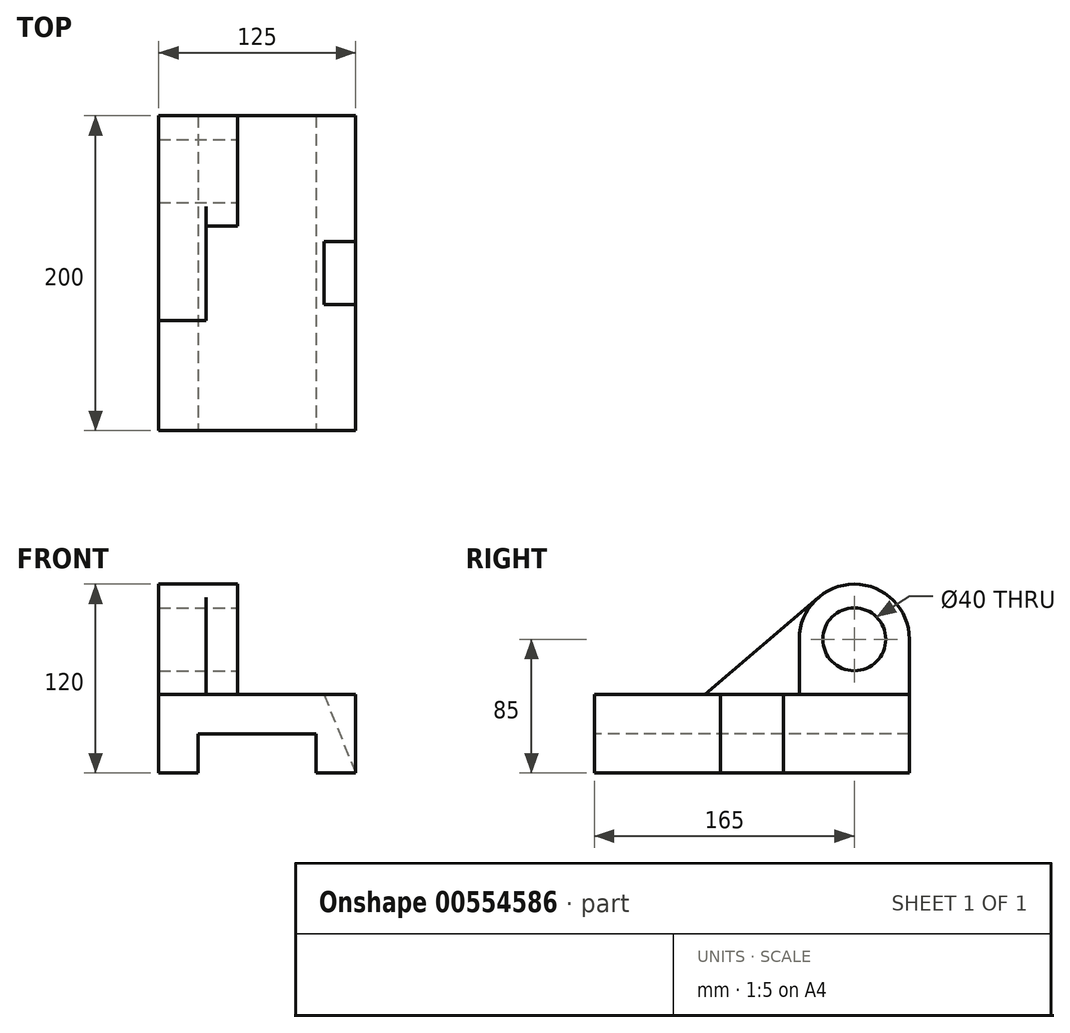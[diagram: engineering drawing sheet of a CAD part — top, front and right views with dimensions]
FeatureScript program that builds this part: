
annotation { "Feature Type Name" : "Feature", "Feature Type Description" : "" }
export const myFeature = defineFeature(function(context is Context, id is Id, definition is map)
    precondition{}
    {
        {
            var Q0;
            Q0=qCreatedBy(makeId("Top.planeOp"),FACE);
            var sketch = newSketch(context, id + "F0", { "sketchPlane" : qUnion([Q0])});
            skLineSegment(sketch, "E0.bottom", {"start": v(61.97, -78.78) * mm, "end": v(-63.03, -78.78) * mm});
            skLineSegment(sketch, "E0.top", {"start": v(61.97, 121.22) * mm, "end": v(-63.03, 121.22) * mm});
            skLineSegment(sketch, "E0.left", {"start": v(61.97, -78.78) * mm, "end": v(61.97, 121.22) * mm});
            skLineSegment(sketch, "E0.right", {"start": v(-63.03, -78.78) * mm, "end": v(-63.03, 121.22) * mm});
            skSolve(sketch);
        }
        {
            var Q0;
            Q0=makeQuery(id+"F0.imprint","IMPRINT",FACE,{"disambiguationData":[TD([[makeQuery(id+"F0.imprint","IMPRINT",EDGE,{"derivedFrom":sQuery(id+"F0.wireOp",EDGE,"E0.bottom")}),-1.0]])]});
            extrude(context, id + "F1", {"entities" : qUnion([Q0]), "depth" : 50 * mm, "offsetDistance" : 25 * mm});
        }
        {
            var Q0;
            Q0=makeQuery(id+"F1.opExtrude","CAP_FACE",FACE,{"disambiguationData":[OSD([sQuery(id+"F0.wireOp",EDGE,"E0.bottom"),sQuery(id+"F0.wireOp",EDGE,"E0.top"),sQuery(id+"F0.wireOp",EDGE,"E0.left"),sQuery(id+"F0.wireOp",EDGE,"E0.right")])],"isStart":false});
            var sketch = newSketch(context, id + "F2", { "sketchPlane" : qUnion([Q0])});
            skLineSegment(sketch, "E1.bottom", {"start": v(-63.03, 121.22) * mm, "end": v(-13.03, 121.22) * mm});
            skLineSegment(sketch, "E1.top", {"start": v(-63.03, 51.22) * mm, "end": v(-13.03, 51.22) * mm});
            skLineSegment(sketch, "E1.left", {"start": v(-63.03, 121.22) * mm, "end": v(-63.03, 51.22) * mm});
            skLineSegment(sketch, "E1.right", {"start": v(-13.03, 121.22) * mm, "end": v(-13.03, 51.22) * mm});
            skSolve(sketch);
        }
        {
            var Q0;
            Q0=makeQuery(id+"F2.imprint","IMPRINT",FACE,{"disambiguationData":[TD([[makeQuery(id+"F2.imprint","IMPRINT",EDGE,{"derivedFrom":sQuery(id+"F2.wireOp",EDGE,"E1.bottom")}),1.0]])]});
            extrude(context, id + "F3", {"entities" : qUnion([Q0]), "operationType" : NewBodyOperationType.ADD, "depth" : 35 * mm, "offsetDistance" : 25 * mm});
        }
        {
            var Q0;
            Q0=makeQuery(id+"F3.opExtrude","SWEPT_FACE",FACE,{"disambiguationData":[OSD([sQuery(id+"F2.wireOp",EDGE,"E1.right")])]});
            var sketch = newSketch(context, id + "F4", { "sketchPlane" : qUnion([Q0])});
            skCircle(sketch, "E2", {"center": v(86.22, 85) * mm, "radius": 35 * mm});
            skSolve(sketch);
        }
        {
            var Q0;
            {var subQ1=sQuery(id+"F2.wireOp",EDGE,"E1.right");var subQ2=makeQuery(id+"F3.opExtrude","CAP_EDGE",EDGE,{"disambiguationData":[OSD([subQ1])],"isStart":false});Q0=makeQuery(id+"F4.imprint","IMPRINT",FACE,{"disambiguationData":[TD([[makeQuery(id+"F4.imprint","IMPRINT",EDGE,{"derivedFrom":subQ2}),-1.0]])]});}
            extrude(context, id + "F5", {"entities" : qUnion([Q0]), "operationType" : NewBodyOperationType.ADD, "oppositeDirection" : true, "depth" : 50 * mm, "offsetDistance" : 25 * mm});
        }
        {
            var Q0;
            {var subQ0=sQuery(id+"F2.wireOp",EDGE,"E1.right");Q0=makeQuery(id+"F5.boolean.opBoolean","MERGE",FACE,{"derivedFrom":[makeQuery(id+"F3.opExtrude","SWEPT_FACE",FACE,{"disambiguationData":[OSD([subQ0])]}),makeQuery(id+"F5.opExtrude","CAP_FACE",FACE,{"disambiguationData":[OSD([subQ0,sQuery(id+"F4.wireOp",EDGE,"E2")])],"isStart":true})]});}
            var sketch = newSketch(context, id + "F6", { "sketchPlane" : qUnion([Q0])});
            skCircle(sketch, "E3", {"center": v(86.22, 85) * mm, "radius": 20 * mm});
            skSolve(sketch);
        }
        {
            var Q0;
            Q0=makeQuery(id+"F6.imprint","IMPRINT",FACE,{"disambiguationData":[TD([[makeQuery(id+"F6.imprint","IMPRINT",EDGE,{"derivedFrom":sQuery(id+"F6.wireOp",EDGE,"E3")}),1.0]])]});
            extrude(context, id + "F7", {"entities" : qUnion([Q0]), "operationType" : NewBodyOperationType.REMOVE, "endBound" : BoundingType.THROUGH_ALL, "oppositeDirection" : true, "depth" : 25 * mm, "offsetDistance" : 25 * mm});
        }
        {
            var Q0;
            Q0=makeQuery(id+"F5.boolean.opBoolean","MERGE",FACE,{"derivedFrom":[makeQuery(id+"F3.boolean.opBoolean","MERGE",FACE,{"derivedFrom":[makeQuery(id+"F1.opExtrude","SWEPT_FACE",FACE,{"disambiguationData":[OSD([sQuery(id+"F0.wireOp",EDGE,"E0.right")])]}),makeQuery(id+"F3.opExtrude","SWEPT_FACE",FACE,{"disambiguationData":[OSD([sQuery(id+"F2.wireOp",EDGE,"E1.left")])]})]}),makeQuery(id+"F5.opExtrude","CAP_FACE",FACE,{"disambiguationData":[OSD([sQuery(id+"F2.wireOp",EDGE,"E1.right"),sQuery(id+"F4.wireOp",EDGE,"E2")])],"isStart":false})]});
            var sketch = newSketch(context, id + "F8", { "sketchPlane" : qUnion([Q0])});
            skLineSegment(sketch, "E4", {"start": v(8.78, 50) * mm, "end": v(-63.51, 111.63) * mm});
            skSolve(sketch);
        }
        {
            var Q0;
            {var subQ0=sQuery(id+"F8.wireOp",EDGE,"E4");Q0=makeQuery(id+"F8.imprint","IMPRINT",FACE,{"disambiguationData":[TD([[makeQuery(id+"F8.imprint","IMPRINT",EDGE,{"derivedFrom":subQ0}),1.0]])]});}
            extrude(context, id + "F9", {"entities" : qUnion([Q0]), "operationType" : NewBodyOperationType.ADD, "oppositeDirection" : true, "depth" : 30 * mm, "offsetDistance" : 25 * mm});
        }
        {
            var Q0;
            Q0=makeQuery(id+"F1.opExtrude","SWEPT_FACE",FACE,{"disambiguationData":[OSD([sQuery(id+"F0.wireOp",EDGE,"E0.bottom")])]});
            var sketch = newSketch(context, id + "F10", { "sketchPlane" : qUnion([Q0])});
            skLineSegment(sketch, "E5.bottom", {"start": v(-38.03, 0) * mm, "end": v(36.97, 0) * mm});
            skLineSegment(sketch, "E5.top", {"start": v(-38.03, 25) * mm, "end": v(36.97, 25) * mm});
            skLineSegment(sketch, "E5.left", {"start": v(-38.03, 0) * mm, "end": v(-38.03, 25) * mm});
            skLineSegment(sketch, "E5.right", {"start": v(36.97, 0) * mm, "end": v(36.97, 25) * mm});
            skSolve(sketch);
        }
        {
            var Q0;
            Q0=makeQuery(id+"F10.imprint","IMPRINT",FACE,{"disambiguationData":[TD([[makeQuery(id+"F10.imprint","IMPRINT",EDGE,{"derivedFrom":sQuery(id+"F10.wireOp",EDGE,"E5.bottom")}),-1.0]])]});
            extrude(context, id + "F11", {"entities" : qUnion([Q0]), "operationType" : NewBodyOperationType.REMOVE, "endBound" : BoundingType.THROUGH_ALL, "oppositeDirection" : true, "depth" : 25 * mm, "offsetDistance" : 25 * mm});
        }
        {
            var Q0;
            Q0=makeQuery(id+"F1.opExtrude","SWEPT_FACE",FACE,{"disambiguationData":[OSD([sQuery(id+"F0.wireOp",EDGE,"E0.left")])]});
            var sketch = newSketch(context, id + "F12", { "sketchPlane" : qUnion([Q0])});
            skLineSegment(sketch, "E6.bottom", {"start": v(1.22, 0) * mm, "end": v(41.22, 0) * mm});
            skLineSegment(sketch, "E6.top", {"start": v(1.22, 50) * mm, "end": v(41.22, 50) * mm});
            skLineSegment(sketch, "E6.left", {"start": v(1.22, 0) * mm, "end": v(1.22, 50) * mm});
            skLineSegment(sketch, "E6.right", {"start": v(41.22, 0) * mm, "end": v(41.22, 50) * mm});
            skSolve(sketch);
        }
        {
            var Q0;
            Q0=makeQuery(id+"F12.imprint","IMPRINT",FACE,{"disambiguationData":[TD([[makeQuery(id+"F12.imprint","IMPRINT",EDGE,{"derivedFrom":sQuery(id+"F12.wireOp",EDGE,"E6.bottom")}),1.0]])]});
            extrude(context, id + "F13", {"entities" : qUnion([Q0]), "operationType" : NewBodyOperationType.REMOVE, "oppositeDirection" : true, "depth" : 20 * mm, "offsetDistance" : 25 * mm});
        }
        {
            var Q0;
            Q0=makeQuery(id+"F13.boolean.opBoolean","COPY",FACE,{"derivedFrom":makeQuery(id+"F13.opExtrude","SWEPT_FACE",FACE,{"disambiguationData":[OSD([sQuery(id+"F12.wireOp",EDGE,"E6.right")])]})});
            var sketch = newSketch(context, id + "F14", { "sketchPlane" : qUnion([Q0])});
            skLineSegment(sketch, "E7", {"start": v(41.97, 50) * mm, "end": v(61.97, 0) * mm});
            skSolve(sketch);
        }
        {
            var Q0;
            Q0=makeQuery(id+"F14.imprint","IMPRINT",FACE,{"disambiguationData":[TD([[makeQuery(id+"F14.imprint","IMPRINT",EDGE,{"derivedFrom":sQuery(id+"F14.wireOp",EDGE,"E7")}),-1.0]])]});
            extrude(context, id + "F15", {"entities" : qUnion([Q0]), "operationType" : NewBodyOperationType.ADD, "depth" : 40 * mm, "offsetDistance" : 25 * mm});
        }
    });
